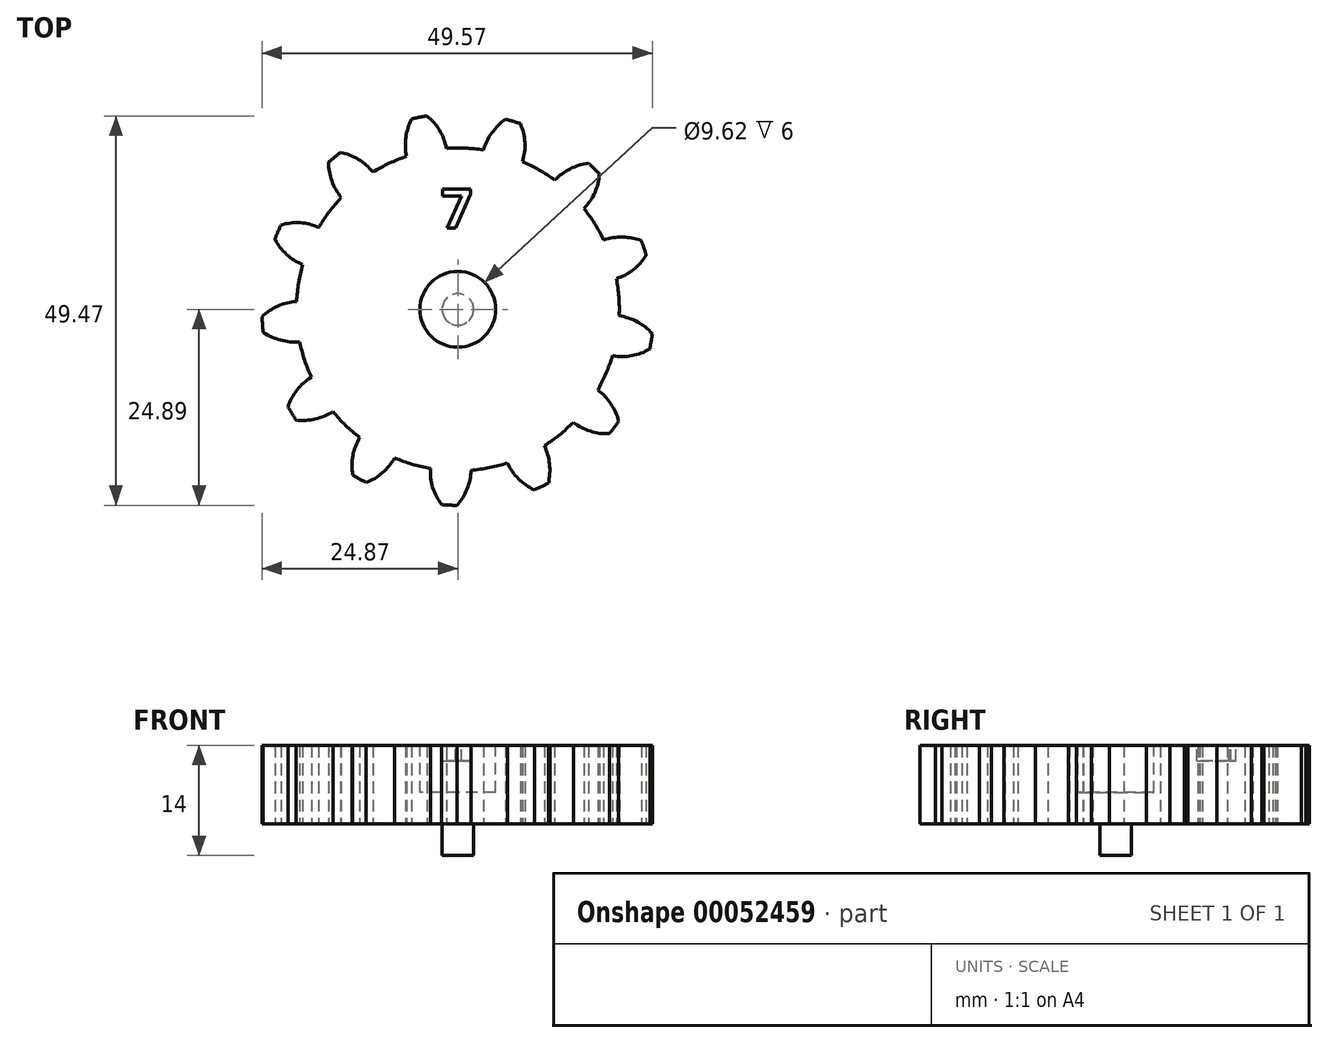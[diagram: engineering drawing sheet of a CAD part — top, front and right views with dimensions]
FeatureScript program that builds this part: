
annotation { "Feature Type Name" : "Feature", "Feature Type Description" : "" }
export const myFeature = defineFeature(function(context is Context, id is Id, definition is map)
    precondition{}
    {
        {
            var Q0;
            Q0=qCreatedBy(makeId("Top.planeOp"),FACE);
            var sketch = newSketch(context, id + "F0", { "sketchPlane" : qUnion([Q0])});
            skCircle(sketch, "E0", {"center": v(0, 0) * mm, "radius": 25.4 * mm, "construction": true});
            skCircle(sketch, "E1", {"center": v(0, 0) * mm, "radius": 24.9 * mm});
            skCircle(sketch, "E2", {"center": v(0, 0) * mm, "radius": 22.13 * mm, "construction": true});
            skCircle(sketch, "E3", {"center": v(0, 0) * mm, "radius": 20.9 * mm, "construction": true});
            skLineSegment(sketch, "E4", {"start": v(0, 20.9) * mm, "end": v(0, 25.4) * mm, "construction": true});
            skLineSegment(sketch, "E5", {"start": v(-6.36, 24.6) * mm, "end": v(-5.23, 20.23) * mm, "construction": true});
            skLineSegment(sketch, "E6", {"start": v(-5.23, 20.23) * mm, "end": v(0, 22.13) * mm, "construction": true});
            skLineSegment(sketch, "E7", {"start": v(-13.83, 20.7) * mm, "end": v(-14.11, 21.12) * mm});
            skLineSegment(sketch, "E8", {"start": v(0, 22.13) * mm, "end": v(6.62, 24.52) * mm, "construction": true});
            skLineSegment(sketch, "E9", {"start": v(10.24, 18.22) * mm, "end": v(3.9, 21.78) * mm, "construction": true});
            skCircle(sketch, "E10", {"center": v(10.24, 18.22) * mm, "radius": 7.26 * mm});
            skLineSegment(sketch, "E11", {"start": v(3.9, 21.78) * mm, "end": v(4.4, 24.5) * mm, "construction": true});
            skLineSegment(sketch, "E12", {"start": v(15.28, 19.65) * mm, "end": v(13.58, 17.47) * mm, "construction": true});
            skLineSegment(sketch, "E13", {"start": v(10.13, 22.74) * mm, "end": v(9, 20.21) * mm, "construction": true});
            skLineSegment(sketch, "E14", {"start": v(3.9, 21.78) * mm, "end": v(10.13, 22.74) * mm, "construction": true});
            skLineSegment(sketch, "E15", {"start": v(13.58, 17.47) * mm, "end": v(10.13, 22.74) * mm, "construction": true});
            skCircle(sketch, "E16", {"center": v(0, 0) * mm, "radius": 20.5 * mm});
            skLineSegment(sketch, "E17", {"start": v(5.68, 19.55) * mm, "end": v(3.26, 20.25) * mm, "construction": true});
            skLineSegment(sketch, "E18", {"start": v(9, 20.21) * mm, "end": v(8.5, 20.25) * mm});
            skLineSegment(sketch, "E19", {"start": v(8.5, 20.25) * mm, "end": v(1.77, 20.83) * mm, "construction": true});
            skCircle(sketch, "E20", {"center": v(1.77, 20.83) * mm, "radius": 6.76 * mm});
            skLineSegment(sketch, "E21", {"start": v(5.68, 19.55) * mm, "end": v(7.21, 24.82) * mm, "construction": true});
            skLineSegment(sketch, "E22", {"start": v(9, 20.21) * mm, "end": v(3.9, 21.78) * mm, "construction": true});
            skSolve(sketch);
        }
        {
            var Q0;
            {var subQ0=sQuery(id+"F0.wireOp",EDGE,"E20");var subQ3=sQuery(id+"F0.wireOp",EDGE,"E10");var subQ4=makeQuery(id+"F0.imprint","INTERSECT",VERTEX,{"disambiguationData":[OD(1.0)],"derivedFrom":[subQ3,subQ0]});Q0=makeQuery(id+"F0.imprint","IMPRINT",FACE,{"disambiguationData":[TD([[makeQuery(id+"F0.imprint","IMPRINT",EDGE,{"disambiguationData":[TD([[subQ4,-1.0]])],"derivedFrom":subQ3}),-1.0]])]});}
            var Q1;
            {var subQ0=sQuery(id+"F0.wireOp",EDGE,"E20");var subQ3=sQuery(id+"F0.wireOp",EDGE,"E10");var subQ4=makeQuery(id+"F0.imprint","INTERSECT",VERTEX,{"disambiguationData":[OD(1.0)],"derivedFrom":[subQ3,subQ0]});Q1=makeQuery(id+"F0.imprint","IMPRINT",FACE,{"disambiguationData":[TD([[makeQuery(id+"F0.imprint","IMPRINT",EDGE,{"disambiguationData":[TD([[subQ4,-1.0]])],"derivedFrom":subQ3}),1.0]])]});}
            var Q2;
            {var subQ1=sQuery(id+"F0.wireOp",EDGE,"E16");var subQ3=sQuery(id+"F0.wireOp",EDGE,"E10");var subQ5=makeQuery(id+"F0.imprint","INTERSECT",VERTEX,{"disambiguationData":[OD(0.0)],"derivedFrom":[subQ3,subQ1]});Q2=makeQuery(id+"F0.imprint","IMPRINT",FACE,{"disambiguationData":[TD([[makeQuery(id+"F0.imprint","IMPRINT",EDGE,{"disambiguationData":[TD([[subQ5,-1.0]])],"derivedFrom":subQ3}),1.0]])]});}
            var Q3;
            {var subQ1=sQuery(id+"F0.wireOp",EDGE,"E16");var subQ3=sQuery(id+"F0.wireOp",EDGE,"E10");var subQ5=makeQuery(id+"F0.imprint","INTERSECT",VERTEX,{"disambiguationData":[OD(0.0)],"derivedFrom":[subQ3,subQ1]});Q3=makeQuery(id+"F0.imprint","IMPRINT",FACE,{"disambiguationData":[TD([[makeQuery(id+"F0.imprint","IMPRINT",EDGE,{"disambiguationData":[TD([[subQ5,-1.0]])],"derivedFrom":subQ3}),-1.0]])]});}
            var Q4;
            {var subQ0=sQuery(id+"F0.wireOp",EDGE,"E20");var subQ3=makeQuery(id+"F0.imprint","IMPRINT",VERTEX,{"derivedFrom":subQ0});Q4=makeQuery(id+"F0.imprint","IMPRINT",FACE,{"disambiguationData":[TD([[makeQuery(id+"F0.imprint","IMPRINT",EDGE,{"disambiguationData":[TD([[subQ3,-1.0]])],"derivedFrom":subQ0}),1.0]])]});}
            extrude(context, id + "F1", {"entities" : qUnion([Q0, Q1, Q2, Q3, Q4]), "depth" : 10 * mm});
        }
        {
            var Q0;
            Q0=makeQuery(id+"F1.opExtrude","SWEPT_BODY",BODY,{"disambiguationData":[OSD([sQuery(id+"F0.wireOp",EDGE,"E1"),sQuery(id+"F0.wireOp",EDGE,"E10"),sQuery(id+"F0.wireOp",EDGE,"E16"),sQuery(id+"F0.wireOp",EDGE,"E20")])]});
            var Q1;
            Q1=makeQuery(id+"F1.opExtrude","CAP_EDGE",EDGE,{"disambiguationData":[OSD([sQuery(id+"F0.wireOp",EDGE,"E16")])],"isStart":false});
            circularPattern(context, id + "F2", {"operationType" : NewBodyOperationType.ADD, "entities" : qUnion([Q0]), "axis" : qUnion([Q1]), "angle" : 360 * degree, "instanceCount" : round(13), "equalSpace" : true});
        }
        {
            var Q0;
            {var subQ0=makeQuery(id+"F1.opExtrude","CAP_FACE",FACE,{"disambiguationData":[OSD([sQuery(id+"F0.wireOp",EDGE,"E1"),sQuery(id+"F0.wireOp",EDGE,"E10"),sQuery(id+"F0.wireOp",EDGE,"E16"),sQuery(id+"F0.wireOp",EDGE,"E20")])],"isStart":false});Q0=makeQuery(id+"F2.boolean.opBoolean","MERGE",FACE,{"derivedFrom":[subQ0,makeQuery(id+"F2.opPattern","COPY",FACE,{"derivedFrom":subQ0,"instanceName":"1"}),makeQuery(id+"F2.opPattern","COPY",FACE,{"derivedFrom":subQ0,"instanceName":"2"}),makeQuery(id+"F2.opPattern","COPY",FACE,{"derivedFrom":subQ0,"instanceName":"3"}),makeQuery(id+"F2.opPattern","COPY",FACE,{"derivedFrom":subQ0,"instanceName":"4"}),makeQuery(id+"F2.opPattern","COPY",FACE,{"derivedFrom":subQ0,"instanceName":"5"}),makeQuery(id+"F2.opPattern","COPY",FACE,{"derivedFrom":subQ0,"instanceName":"6"}),makeQuery(id+"F2.opPattern","COPY",FACE,{"derivedFrom":subQ0,"instanceName":"7"}),makeQuery(id+"F2.opPattern","COPY",FACE,{"derivedFrom":subQ0,"instanceName":"8"}),makeQuery(id+"F2.opPattern","COPY",FACE,{"derivedFrom":subQ0,"instanceName":"9"}),makeQuery(id+"F2.opPattern","COPY",FACE,{"derivedFrom":subQ0,"instanceName":"10"}),makeQuery(id+"F2.opPattern","COPY",FACE,{"derivedFrom":subQ0,"instanceName":"11"}),makeQuery(id+"F2.opPattern","COPY",FACE,{"derivedFrom":subQ0,"instanceName":"12"})]});}
            var sketch = newSketch(context, id + "F3", { "sketchPlane" : qUnion([Q0])});
            skPoint(sketch, "E23.rect.middle", {"position": v(0, 14.76) * mm});
            skCircle(sketch, "E24.0", {"center": v(0, 0) * mm, "radius": 4.81 * mm});
            skSolve(sketch);
        }
        {
            var Q0;
            Q0=makeQuery(id+"F3.imprint","IMPRINT",FACE,{"disambiguationData":[TD([[makeQuery(id+"F3.imprint","IMPRINT",EDGE,{"derivedFrom":sQuery(id+"F3.wireOp",EDGE,"E24.0")}),1.0]])]});
            extrude(context, id + "F4", {"entities" : qUnion([Q0]), "operationType" : NewBodyOperationType.REMOVE, "oppositeDirection" : true, "depth" : 6 * mm});
        }
        {
            var Q0;
            {var subQ0=makeQuery(id+"F1.opExtrude","CAP_FACE",FACE,{"disambiguationData":[OSD([sQuery(id+"F0.wireOp",EDGE,"E1"),sQuery(id+"F0.wireOp",EDGE,"E10"),sQuery(id+"F0.wireOp",EDGE,"E16"),sQuery(id+"F0.wireOp",EDGE,"E20")])],"isStart":true});Q0=makeQuery(id+"F2.boolean.opBoolean","MERGE",FACE,{"derivedFrom":[subQ0,makeQuery(id+"F2.opPattern","COPY",FACE,{"derivedFrom":subQ0,"instanceName":"1"}),makeQuery(id+"F2.opPattern","COPY",FACE,{"derivedFrom":subQ0,"instanceName":"2"}),makeQuery(id+"F2.opPattern","COPY",FACE,{"derivedFrom":subQ0,"instanceName":"3"}),makeQuery(id+"F2.opPattern","COPY",FACE,{"derivedFrom":subQ0,"instanceName":"4"}),makeQuery(id+"F2.opPattern","COPY",FACE,{"derivedFrom":subQ0,"instanceName":"5"}),makeQuery(id+"F2.opPattern","COPY",FACE,{"derivedFrom":subQ0,"instanceName":"6"}),makeQuery(id+"F2.opPattern","COPY",FACE,{"derivedFrom":subQ0,"instanceName":"7"}),makeQuery(id+"F2.opPattern","COPY",FACE,{"derivedFrom":subQ0,"instanceName":"8"}),makeQuery(id+"F2.opPattern","COPY",FACE,{"derivedFrom":subQ0,"instanceName":"9"}),makeQuery(id+"F2.opPattern","COPY",FACE,{"derivedFrom":subQ0,"instanceName":"10"}),makeQuery(id+"F2.opPattern","COPY",FACE,{"derivedFrom":subQ0,"instanceName":"11"}),makeQuery(id+"F2.opPattern","COPY",FACE,{"derivedFrom":subQ0,"instanceName":"12"})]});}
            var sketch = newSketch(context, id + "F5", { "sketchPlane" : qUnion([Q0])});
            skCircle(sketch, "E25", {"center": v(0, 0) * mm, "radius": 2 * mm});
            skSolve(sketch);
        }
        {
            var Q0;
            Q0=qSketchRegion(id+"F5",true);
            extrude(context, id + "F6", {"entities" : qUnion([Q0]), "operationType" : NewBodyOperationType.ADD, "depth" : 4 * mm});
        }
        {
            var Q0;
            {var subQ0=makeQuery(id+"F1.opExtrude","CAP_FACE",FACE,{"disambiguationData":[OSD([sQuery(id+"F0.wireOp",EDGE,"E1"),sQuery(id+"F0.wireOp",EDGE,"E10"),sQuery(id+"F0.wireOp",EDGE,"E16"),sQuery(id+"F0.wireOp",EDGE,"E20")])],"isStart":false});Q0=makeQuery(id+"F2.boolean.opBoolean","MERGE",FACE,{"derivedFrom":[subQ0,makeQuery(id+"F2.opPattern","COPY",FACE,{"derivedFrom":subQ0,"instanceName":"1"}),makeQuery(id+"F2.opPattern","COPY",FACE,{"derivedFrom":subQ0,"instanceName":"2"}),makeQuery(id+"F2.opPattern","COPY",FACE,{"derivedFrom":subQ0,"instanceName":"3"}),makeQuery(id+"F2.opPattern","COPY",FACE,{"derivedFrom":subQ0,"instanceName":"4"}),makeQuery(id+"F2.opPattern","COPY",FACE,{"derivedFrom":subQ0,"instanceName":"5"}),makeQuery(id+"F2.opPattern","COPY",FACE,{"derivedFrom":subQ0,"instanceName":"6"}),makeQuery(id+"F2.opPattern","COPY",FACE,{"derivedFrom":subQ0,"instanceName":"7"}),makeQuery(id+"F2.opPattern","COPY",FACE,{"derivedFrom":subQ0,"instanceName":"8"}),makeQuery(id+"F2.opPattern","COPY",FACE,{"derivedFrom":subQ0,"instanceName":"9"}),makeQuery(id+"F2.opPattern","COPY",FACE,{"derivedFrom":subQ0,"instanceName":"10"}),makeQuery(id+"F2.opPattern","COPY",FACE,{"derivedFrom":subQ0,"instanceName":"11"}),makeQuery(id+"F2.opPattern","COPY",FACE,{"derivedFrom":subQ0,"instanceName":"12"})]});}
            var sketch = newSketch(context, id + "F7", { "sketchPlane" : qUnion([Q0])});
            skText(sketch, "E26", { "text": "7", "fontName": "OpenSans-Bold.ttf"});
            skPoint(sketch, "E27.start.orphan", {"position": v(0, 0) * mm});
            const initialGuessF7  = {"E26": [-0.00215, 0.01031, 1, 0, 0.00503]};
            skSetInitialGuess(sketch, initialGuessF7);
            skSolve(sketch);
        }
        {
            var Q0;
            Q0=qSketchRegion(id+"F7",true);
            extrude(context, id + "F8", {"entities" : qUnion([Q0]), "operationType" : NewBodyOperationType.REMOVE, "oppositeDirection" : true, "depth" : 2 * mm});
        }
    });
